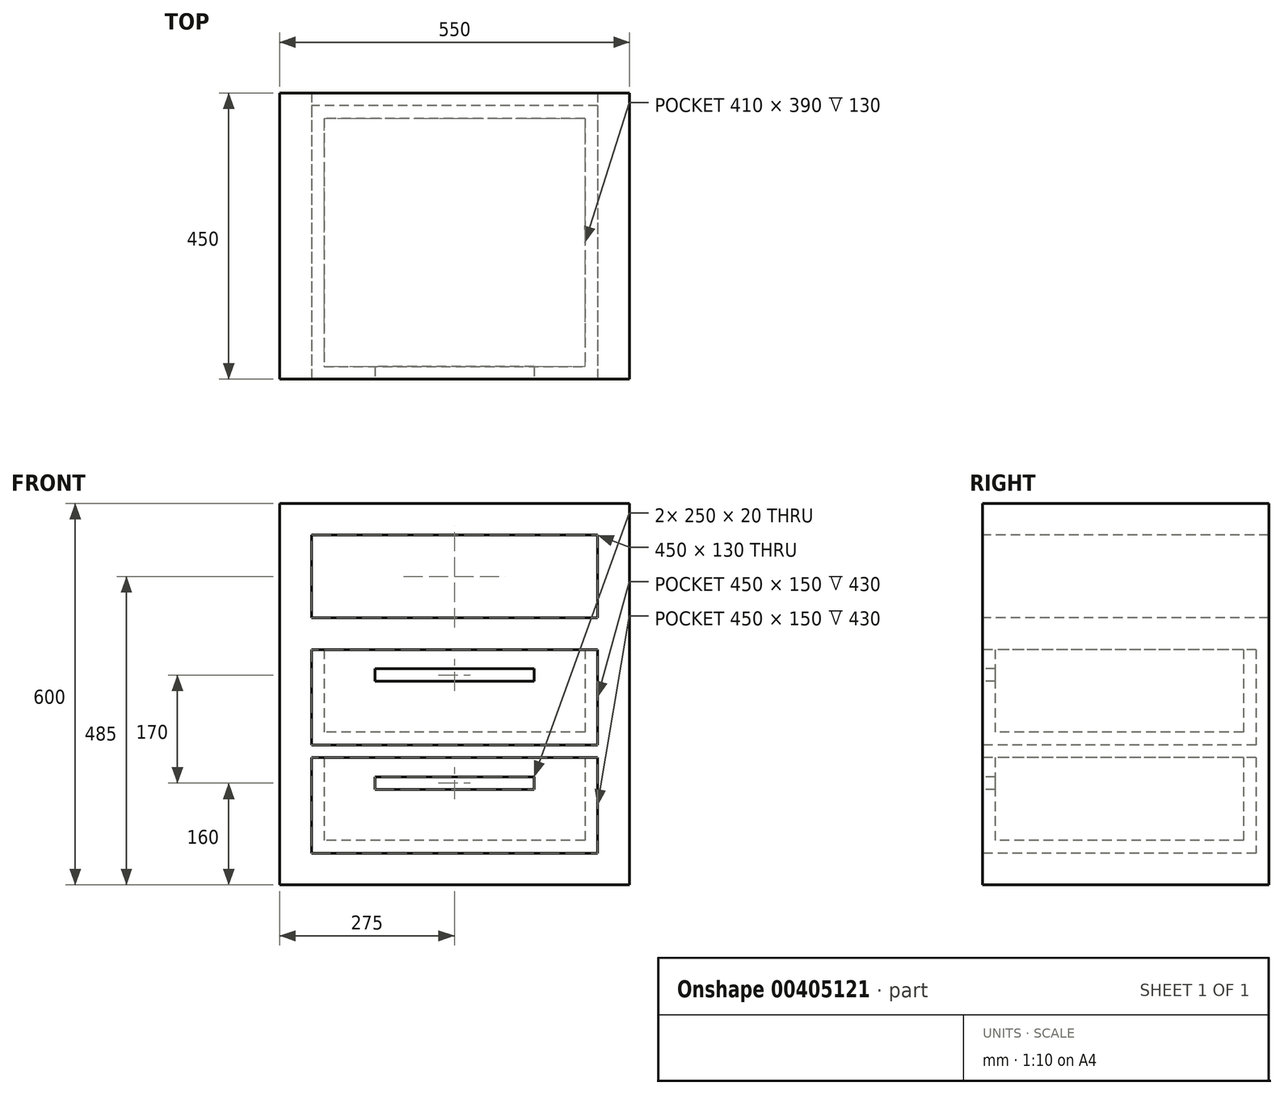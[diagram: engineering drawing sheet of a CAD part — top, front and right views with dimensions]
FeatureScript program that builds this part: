
annotation { "Feature Type Name" : "Feature", "Feature Type Description" : "" }
export const myFeature = defineFeature(function(context is Context, id is Id, definition is map)
    precondition{}
    {
        {
            var Q0;
            Q0=qCreatedBy(makeId("Top.planeOp"),FACE);
            var sketch = newSketch(context, id + "F0", { "sketchPlane" : qUnion([Q0])});
            skLineSegment(sketch, "E0.bottom", {"start": v(-275, -225) * mm, "end": v(275, -225) * mm});
            skLineSegment(sketch, "E0.top", {"start": v(-275, 225) * mm, "end": v(275, 225) * mm});
            skLineSegment(sketch, "E0.left", {"start": v(-275, -225) * mm, "end": v(-275, 225) * mm});
            skLineSegment(sketch, "E0.right", {"start": v(275, -225) * mm, "end": v(275, 225) * mm});
            skLineSegment(sketch, "E1", {"start": v(0, -116.67) * mm, "end": v(0, 150) * mm, "construction": true});
            skLineSegment(sketch, "E2", {"start": v(-153.33, 0) * mm, "end": v(170, 0) * mm, "construction": true});
            skSolve(sketch);
        }
        {
            var Q0;
            Q0=makeQuery(id+"F0.imprint","IMPRINT",FACE,{"disambiguationData":[TD([[makeQuery(id+"F0.imprint","IMPRINT",EDGE,{"derivedFrom":sQuery(id+"F0.wireOp",EDGE,"E0.bottom")}),1.0]])]});
            extrude(context, id + "F1", {"entities" : qUnion([Q0]), "depth" : 600 * mm});
        }
        {
            var Q0;
            Q0=makeQuery(id+"F1.opExtrude","SWEPT_FACE",FACE,{"disambiguationData":[OSD([sQuery(id+"F0.wireOp",EDGE,"E0.bottom")])]});
            var sketch = newSketch(context, id + "F2", { "sketchPlane" : qUnion([Q0])});
            skLineSegment(sketch, "E3.bottom", {"start": v(-225, 50) * mm, "end": v(225, 50) * mm});
            skLineSegment(sketch, "E3.top", {"start": v(-225, 200) * mm, "end": v(225, 200) * mm});
            skLineSegment(sketch, "E3.left", {"start": v(-225, 50) * mm, "end": v(-225, 200) * mm});
            skLineSegment(sketch, "E3.right", {"start": v(225, 50) * mm, "end": v(225, 200) * mm});
            skLineSegment(sketch, "E4.bottom", {"start": v(-225, 220) * mm, "end": v(225, 220) * mm});
            skLineSegment(sketch, "E4.top", {"start": v(-225, 370) * mm, "end": v(225, 370) * mm});
            skLineSegment(sketch, "E4.left", {"start": v(-225, 220) * mm, "end": v(-225, 370) * mm});
            skLineSegment(sketch, "E4.right", {"start": v(225, 220) * mm, "end": v(225, 370) * mm});
            skPoint(sketch, "E5.oppositeSnap0", {"position": v(225, 295) * mm});
            skLineSegment(sketch, "E5.bottom", {"start": v(-225, 420) * mm, "end": v(225, 420) * mm});
            skLineSegment(sketch, "E5.top", {"start": v(-225, 550) * mm, "end": v(225, 550) * mm});
            skLineSegment(sketch, "E5.left", {"start": v(-225, 420) * mm, "end": v(-225, 550) * mm});
            skLineSegment(sketch, "E5.right", {"start": v(225, 420) * mm, "end": v(225, 550) * mm});
            skSolve(sketch);
        }
        {
            var Q0;
            Q0=makeQuery(id+"F2.imprint","IMPRINT",FACE,{"disambiguationData":[TD([[makeQuery(id+"F2.imprint","IMPRINT",EDGE,{"derivedFrom":sQuery(id+"F2.wireOp",EDGE,"E3.bottom")}),1.0]])]});
            var Q1;
            Q1=makeQuery(id+"F2.imprint","IMPRINT",FACE,{"disambiguationData":[TD([[makeQuery(id+"F2.imprint","IMPRINT",EDGE,{"derivedFrom":sQuery(id+"F2.wireOp",EDGE,"E4.bottom")}),1.0]])]});
            var Q2;
            Q2=makeQuery(id+"F2.imprint","IMPRINT",FACE,{"disambiguationData":[TD([[makeQuery(id+"F2.imprint","IMPRINT",EDGE,{"derivedFrom":sQuery(id+"F2.wireOp",EDGE,"E5.bottom")}),1.0]])]});
            extrude(context, id + "F3", {"entities" : qUnion([Q0, Q1, Q2]), "operationType" : NewBodyOperationType.REMOVE, "oppositeDirection" : true, "depth" : 430 * mm});
        }
        {
            var Q0;
            Q0=makeQuery(id+"F3.boolean.opBoolean","COPY",FACE,{"derivedFrom":makeQuery(id+"F3.opExtrude","CAP_FACE",FACE,{"disambiguationData":[OSD([sQuery(id+"F2.wireOp",EDGE,"E5.bottom"),sQuery(id+"F2.wireOp",EDGE,"E5.top"),sQuery(id+"F2.wireOp",EDGE,"E5.left"),sQuery(id+"F2.wireOp",EDGE,"E5.right")])],"isStart":false})});
            extrude(context, id + "F4", {"entities" : qUnion([Q0]), "operationType" : NewBodyOperationType.REMOVE, "endBound" : BoundingType.THROUGH_ALL, "oppositeDirection" : true, "depth" : 25 * mm});
        }
        {
            var Q0;
            Q0=makeQuery(id+"F2.imprint","IMPRINT",FACE,{"disambiguationData":[TD([[makeQuery(id+"F2.imprint","IMPRINT",EDGE,{"derivedFrom":sQuery(id+"F2.wireOp",EDGE,"E3.bottom")}),1.0]])]});
            var Q1;
            Q1=makeQuery(id+"F2.imprint","IMPRINT",FACE,{"disambiguationData":[TD([[makeQuery(id+"F2.imprint","IMPRINT",EDGE,{"derivedFrom":sQuery(id+"F2.wireOp",EDGE,"E4.bottom")}),1.0]])]});
            var Q2;
            Q2=makeQuery(id+"F3.boolean.opBoolean","COPY",FACE,{"derivedFrom":makeQuery(id+"F3.opExtrude","CAP_FACE",FACE,{"disambiguationData":[OSD([sQuery(id+"F2.wireOp",EDGE,"E4.bottom"),sQuery(id+"F2.wireOp",EDGE,"E4.top"),sQuery(id+"F2.wireOp",EDGE,"E4.left"),sQuery(id+"F2.wireOp",EDGE,"E4.right")])],"isStart":false})});
            extrude(context, id + "F5", {"entities" : qUnion([Q0, Q1]), "endBound" : BoundingType.UP_TO_SURFACE, "oppositeDirection" : true, "endBoundEntityFace" : qUnion([Q2]), "depth" : 25 * mm});
        }
        {
            var Q0;
            Q0=makeQuery(id+"F5.opExtrude","SWEPT_FACE",FACE,{"disambiguationData":[OSD([sQuery(id+"F2.wireOp",EDGE,"E4.top")])]});
            var Q1;
            Q1=makeQuery(id+"F5.opExtrude","SWEPT_FACE",FACE,{"disambiguationData":[OSD([sQuery(id+"F2.wireOp",EDGE,"E3.top")])]});
            shell(context, id + "F6", {"entities" : qUnion([Q0, Q1]), "thickness" : 20 * mm});
        }
        {
            var Q0;
            Q0=makeQuery(id+"F5.opExtrude","CAP_FACE",FACE,{"disambiguationData":[OSD([sQuery(id+"F2.wireOp",EDGE,"E4.bottom"),sQuery(id+"F2.wireOp",EDGE,"E4.top"),sQuery(id+"F2.wireOp",EDGE,"E4.left"),sQuery(id+"F2.wireOp",EDGE,"E4.right")])],"isStart":true});
            var sketch = newSketch(context, id + "F7", { "sketchPlane" : qUnion([Q0])});
            skLineSegment(sketch, "E6.bottom", {"start": v(-125, 340) * mm, "end": v(125, 340) * mm});
            skLineSegment(sketch, "E6.top", {"start": v(-125, 320) * mm, "end": v(125, 320) * mm});
            skLineSegment(sketch, "E6.left", {"start": v(-125, 340) * mm, "end": v(-125, 320) * mm});
            skLineSegment(sketch, "E6.right", {"start": v(125, 340) * mm, "end": v(125, 320) * mm});
            skLineSegment(sketch, "E7.bottom", {"start": v(-125, 170) * mm, "end": v(125, 170) * mm});
            skLineSegment(sketch, "E7.top", {"start": v(-125, 150) * mm, "end": v(125, 150) * mm});
            skLineSegment(sketch, "E7.left", {"start": v(-125, 170) * mm, "end": v(-125, 150) * mm});
            skLineSegment(sketch, "E7.right", {"start": v(125, 170) * mm, "end": v(125, 150) * mm});
            skLineSegment(sketch, "E8", {"start": v(0, 268.36) * mm, "end": v(0, 294.13) * mm, "construction": true});
            skSolve(sketch);
        }
        {
            var Q0;
            Q0=makeQuery(id+"F7.imprint","IMPRINT",FACE,{"disambiguationData":[TD([[makeQuery(id+"F7.imprint","IMPRINT",EDGE,{"derivedFrom":sQuery(id+"F7.wireOp",EDGE,"E6.bottom")}),-1.0]])]});
            var Q1;
            Q1=makeQuery(id+"F7.imprint","IMPRINT",FACE,{"disambiguationData":[TD([[makeQuery(id+"F7.imprint","IMPRINT",EDGE,{"derivedFrom":sQuery(id+"F7.wireOp",EDGE,"E7.bottom")}),-1.0]])]});
            extrude(context, id + "F8", {"entities" : qUnion([Q0, Q1]), "operationType" : NewBodyOperationType.REMOVE, "endBound" : BoundingType.UP_TO_NEXT, "oppositeDirection" : true, "depth" : 25 * mm});
        }
    });
